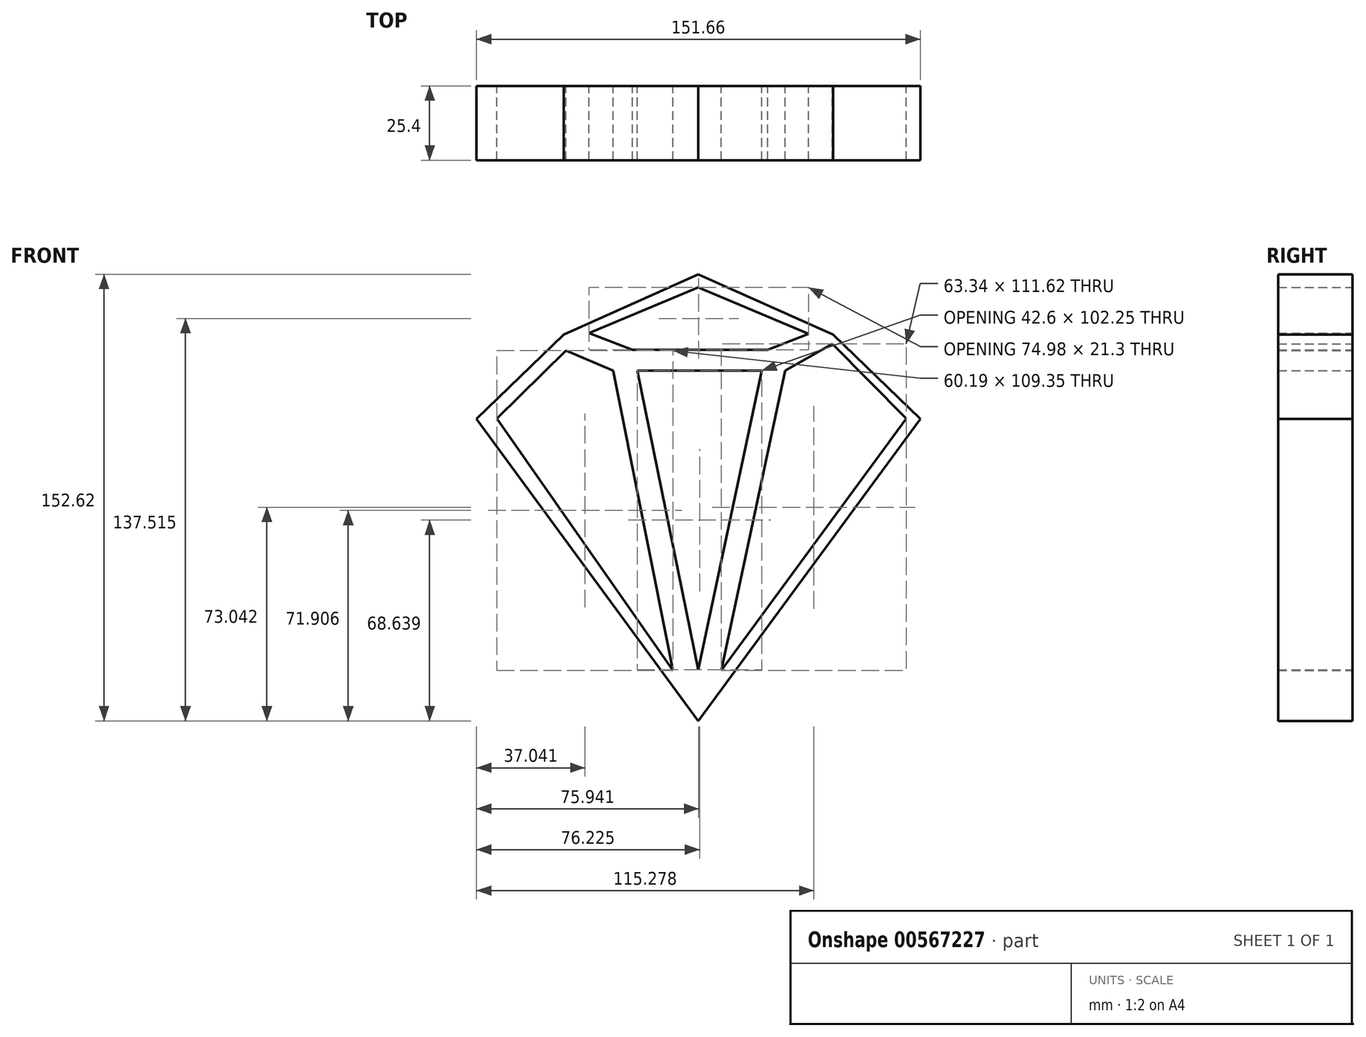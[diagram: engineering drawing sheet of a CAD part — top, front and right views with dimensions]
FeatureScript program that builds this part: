
annotation { "Feature Type Name" : "Feature", "Feature Type Description" : "" }
export const myFeature = defineFeature(function(context is Context, id is Id, definition is map)
    precondition{}
    {
        {
            var Q0;
            Q0=qCreatedBy(makeId("Front.planeOp"),FACE);
            var sketch = newSketch(context, id + "F0", { "sketchPlane" : qUnion([Q0])});
            skLineSegment(sketch, "E0", {"start": v(0, -76.19) * mm, "end": v(75.95, 26.99) * mm});
            skLineSegment(sketch, "E1", {"start": v(75.95, 26.99) * mm, "end": v(46.1, 55.89) * mm});
            skLineSegment(sketch, "E2", {"start": v(46.1, 55.89) * mm, "end": v(0, 76.43) * mm});
            skLineSegment(sketch, "E3", {"start": v(0, 76.43) * mm, "end": v(-45.86, 55.89) * mm});
            skLineSegment(sketch, "E4", {"start": v(-45.86, 55.89) * mm, "end": v(-75.71, 26.99) * mm});
            skLineSegment(sketch, "E5", {"start": v(-75.71, 26.99) * mm, "end": v(0, -76.19) * mm});
            skLineSegment(sketch, "E6", {"start": v(46.1, 55.89) * mm, "end": v(26.63, 47.16) * mm});
            skLineSegment(sketch, "E7", {"start": v(26.63, 47.16) * mm, "end": v(-25.32, 47.16) * mm});
            skLineSegment(sketch, "E8", {"start": v(-25.32, 47.16) * mm, "end": v(-45.86, 55.89) * mm});
            skLineSegment(sketch, "E9", {"start": v(-25.32, 65.09) * mm, "end": v(-15.57, 60.74) * mm});
            skLineSegment(sketch, "E10", {"start": v(-15.57, 60.74) * mm, "end": v(16, 60.74) * mm});
            skLineSegment(sketch, "E11", {"start": v(16, 60.74) * mm, "end": v(25.57, 65.03) * mm});
            skLineSegment(sketch, "E12", {"start": v(16, 60.74) * mm, "end": v(26.63, 47.16) * mm});
            skLineSegment(sketch, "E13", {"start": v(26.63, 47.16) * mm, "end": v(0, -76.19) * mm});
            skLineSegment(sketch, "E14", {"start": v(-15.57, 60.74) * mm, "end": v(-25.32, 47.16) * mm});
            skLineSegment(sketch, "E15", {"start": v(-25.32, 47.16) * mm, "end": v(0, -76.19) * mm});
            skSolve(sketch);
        }
        {
            var Q0;
            Q0=qCreatedBy(makeId("Front.planeOp"),FACE);
            var sketch = newSketch(context, id + "F1", { "sketchPlane" : qUnion([Q0])});
            skLineSegment(sketch, "E16", {"start": v(45.96, 52.66) * mm, "end": v(71.24, 27.1) * mm});
            skLineSegment(sketch, "E17", {"start": v(71.24, 27.1) * mm, "end": v(7.9, -58.96) * mm});
            skLineSegment(sketch, "E18", {"start": v(7.9, -58.96) * mm, "end": v(29.77, 43.57) * mm});
            skLineSegment(sketch, "E19", {"start": v(29.77, 43.57) * mm, "end": v(45.96, 52.66) * mm});
            skLineSegment(sketch, "E20", {"start": v(-8.57, -58.96) * mm, "end": v(-29.02, 43.57) * mm});
            skLineSegment(sketch, "E21", {"start": v(-29.02, 43.57) * mm, "end": v(-45.21, 50.4) * mm});
            skLineSegment(sketch, "E22", {"start": v(-45.21, 50.4) * mm, "end": v(-68.76, 27.1) * mm});
            skLineSegment(sketch, "E23", {"start": v(-68.76, 27.1) * mm, "end": v(-8.57, -58.96) * mm});
            skSolve(sketch);
        }
        {
            var Q0;
            Q0=qCreatedBy(makeId("Front.planeOp"),FACE);
            var sketch = newSketch(context, id + "F2", { "sketchPlane" : qUnion([Q0])});
            skLineSegment(sketch, "E24", {"start": v(-37.26, 56.35) * mm, "end": v(0, 71.98) * mm});
            skLineSegment(sketch, "E25", {"start": v(0, 71.98) * mm, "end": v(37.72, 56.07) * mm});
            skLineSegment(sketch, "E26", {"start": v(37.72, 56.07) * mm, "end": v(23.8, 50.67) * mm});
            skLineSegment(sketch, "E27", {"start": v(23.8, 50.67) * mm, "end": v(-22.5, 50.67) * mm});
            skLineSegment(sketch, "E28", {"start": v(-22.5, 50.67) * mm, "end": v(-37.26, 56.35) * mm});
            skLineSegment(sketch, "E29", {"start": v(-20.79, 43.57) * mm, "end": v(21.82, 43.57) * mm});
            skLineSegment(sketch, "E30", {"start": v(21.82, 43.57) * mm, "end": v(0, -58.68) * mm});
            skLineSegment(sketch, "E31", {"start": v(0, -58.68) * mm, "end": v(-20.79, 43.57) * mm});
            skSolve(sketch);
        }
        {
            var Q0;
            Q0=makeQuery(id+"F0.imprint","IMPRINT",FACE,{"disambiguationData":[TD([[makeQuery(id+"F0.imprint","IMPRINT",EDGE,{"derivedFrom":sQuery(id+"F0.wireOp",EDGE,"E4")}),1.0]])]});
            var Q1;
            Q1=makeQuery(id+"F0.imprint","IMPRINT",FACE,{"disambiguationData":[TD([[makeQuery(id+"F0.imprint","IMPRINT",EDGE,{"derivedFrom":sQuery(id+"F0.wireOp",EDGE,"E0")}),1.0]])]});
            var Q2;
            Q2=makeQuery(id+"F0.imprint","IMPRINT",FACE,{"disambiguationData":[TD([[makeQuery(id+"F0.imprint","IMPRINT",EDGE,{"derivedFrom":sQuery(id+"F0.wireOp",EDGE,"E7")}),1.0]])]});
            var Q3;
            {var subQ0=sQuery(id+"F0.wireOp",EDGE,"E8");Q3=makeQuery(id+"F0.imprint","IMPRINT",FACE,{"disambiguationData":[TD([[makeQuery(id+"F0.imprint","IMPRINT",EDGE,{"derivedFrom":subQ0}),-1.0]])]});}
            var Q4;
            {var subQ0=sQuery(id+"F0.wireOp",EDGE,"E9");Q4=makeQuery(id+"F0.imprint","IMPRINT",FACE,{"disambiguationData":[TD([[makeQuery(id+"F0.imprint","IMPRINT",EDGE,{"derivedFrom":subQ0}),1.0]])]});}
            var Q5;
            {var subQ0=sQuery(id+"F0.wireOp",EDGE,"E6");Q5=makeQuery(id+"F0.imprint","IMPRINT",FACE,{"disambiguationData":[TD([[makeQuery(id+"F0.imprint","IMPRINT",EDGE,{"derivedFrom":subQ0}),-1.0]])]});}
            var Q6;
            Q6=makeQuery(id+"F0.imprint","IMPRINT",FACE,{"disambiguationData":[TD([[makeQuery(id+"F0.imprint","IMPRINT",EDGE,{"derivedFrom":sQuery(id+"F0.wireOp",EDGE,"E7")}),-1.0]])]});
            extrude(context, id + "F3", {"entities" : qUnion([Q0, Q1, Q2, Q3, Q4, Q5, Q6]), "depth" : 25.4 * mm, "offsetDistance" : 25.4 * mm});
        }
        {
            var Q0;
            Q0=makeQuery(id+"F1.imprint","IMPRINT",FACE,{"disambiguationData":[TD([[makeQuery(id+"F1.imprint","IMPRINT",EDGE,{"derivedFrom":sQuery(id+"F1.wireOp",EDGE,"E20")}),1.0]])]});
            var Q1;
            Q1=makeQuery(id+"F2.imprint","IMPRINT",FACE,{"disambiguationData":[TD([[makeQuery(id+"F2.imprint","IMPRINT",EDGE,{"derivedFrom":sQuery(id+"F2.wireOp",EDGE,"E29")}),-1.0]])]});
            var Q2;
            Q2=makeQuery(id+"F1.imprint","IMPRINT",FACE,{"disambiguationData":[TD([[makeQuery(id+"F1.imprint","IMPRINT",EDGE,{"derivedFrom":sQuery(id+"F1.wireOp",EDGE,"E16")}),-1.0]])]});
            var Q3;
            Q3=makeQuery(id+"F2.imprint","IMPRINT",FACE,{"disambiguationData":[TD([[makeQuery(id+"F2.imprint","IMPRINT",EDGE,{"derivedFrom":sQuery(id+"F2.wireOp",EDGE,"E24")}),-1.0]])]});
            extrude(context, id + "F4", {"entities" : qUnion([Q0, Q1, Q2, Q3]), "operationType" : NewBodyOperationType.REMOVE, "depth" : 30.48 * mm, "offsetDistance" : 25.4 * mm});
        }
        {
            var Q0;
            Q0=qCreatedBy(makeId("Front.planeOp"),FACE);
            var sketch = newSketch(context, id + "F5", { "sketchPlane" : qUnion([Q0])});
            skLineSegment(sketch, "E32", {"start": v(-44.93, 45) * mm, "end": v(-62.82, 26.25) * mm});
            skLineSegment(sketch, "E33", {"start": v(-62.82, 26.25) * mm, "end": v(-17.95, -37.37) * mm});
            skLineSegment(sketch, "E34", {"start": v(-17.95, -37.37) * mm, "end": v(-33.28, 39.88) * mm});
            skLineSegment(sketch, "E35", {"start": v(-33.28, 39.88) * mm, "end": v(-44.93, 45) * mm});
            skSolve(sketch);
        }
        {
            var Q0;
            Q0=qCreatedBy(makeId("Front.planeOp"),FACE);
            var sketch = newSketch(context, id + "F6", { "sketchPlane" : qUnion([Q0])});
            skLineSegment(sketch, "E36", {"start": v(-15.4, 39.03) * mm, "end": v(16.42, 39.03) * mm});
            skLineSegment(sketch, "E37", {"start": v(16.42, 39.03) * mm, "end": v(0, -39.36) * mm});
            skLineSegment(sketch, "E38", {"start": v(0, -39.36) * mm, "end": v(-15.4, 39.03) * mm});
            skLineSegment(sketch, "E39", {"start": v(44.82, 46.7) * mm, "end": v(33.18, 39.03) * mm});
            skLineSegment(sketch, "E40", {"start": v(33.18, 39.03) * mm, "end": v(16.42, -39.36) * mm});
            skLineSegment(sketch, "E41", {"start": v(16.42, -39.36) * mm, "end": v(64.42, 26.82) * mm});
            skLineSegment(sketch, "E42", {"start": v(64.42, 26.82) * mm, "end": v(44.82, 46.7) * mm});
            skSolve(sketch);
        }
        {
            var Q0;
            Q0=makeQuery(id+"F5.imprint","IMPRINT",FACE,{"disambiguationData":[TD([[makeQuery(id+"F5.imprint","IMPRINT",EDGE,{"derivedFrom":sQuery(id+"F5.wireOp",EDGE,"E32")}),1.0]])]});
            var Q1;
            Q1=makeQuery(id+"F6.imprint","IMPRINT",FACE,{"disambiguationData":[TD([[makeQuery(id+"F6.imprint","IMPRINT",EDGE,{"derivedFrom":sQuery(id+"F6.wireOp",EDGE,"E36")}),-1.0]])]});
            var Q2;
            Q2=makeQuery(id+"F6.imprint","IMPRINT",FACE,{"disambiguationData":[TD([[makeQuery(id+"F6.imprint","IMPRINT",EDGE,{"derivedFrom":sQuery(id+"F6.wireOp",EDGE,"E39")}),1.0]])]});
            extrude(context, id + "F7", {"entities" : qUnion([Q0, Q1, Q2]), "operationType" : NewBodyOperationType.REMOVE, "depth" : 50.8 * mm, "offsetDistance" : 25.4 * mm});
        }
    });
